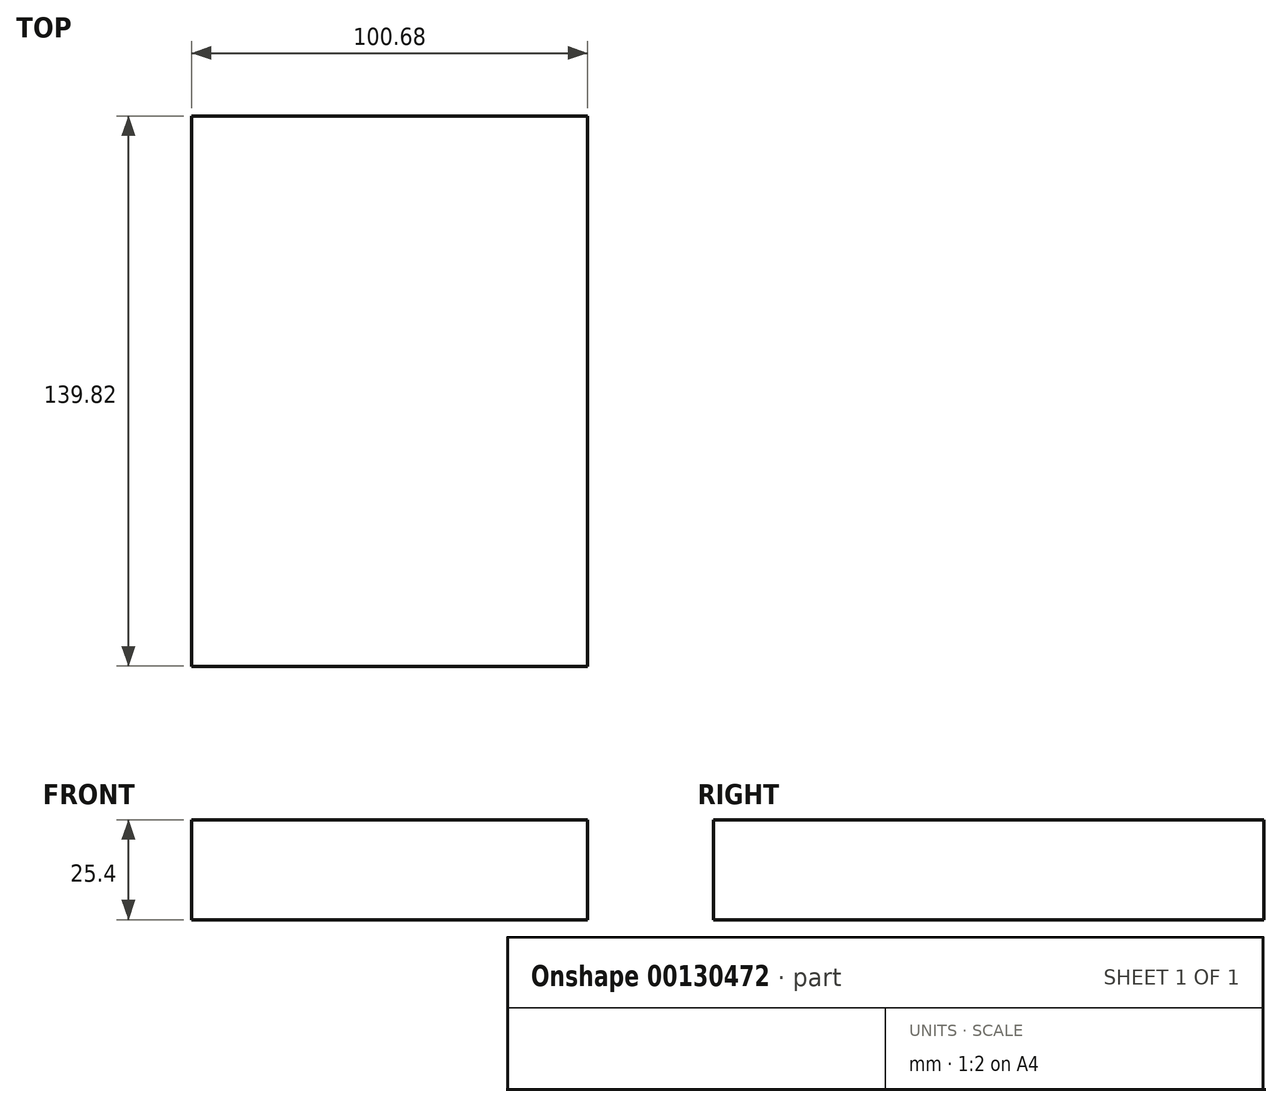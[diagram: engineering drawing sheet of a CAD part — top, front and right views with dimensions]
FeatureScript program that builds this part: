
annotation { "Feature Type Name" : "Feature", "Feature Type Description" : "" }
export const myFeature = defineFeature(function(context is Context, id is Id, definition is map)
    precondition{}
    {
        {
            var Q0;
            Q0=qCreatedBy(makeId("Top.planeOp"),FACE);
            var sketch = newSketch(context, id + "F0", { "sketchPlane" : qUnion([Q0])});
            skLineSegment(sketch, "E0.bottom", {"start": v(-54.6, -68.28) * mm, "end": v(46.08, -68.28) * mm});
            skLineSegment(sketch, "E0.top", {"start": v(-54.6, 71.54) * mm, "end": v(46.08, 71.54) * mm});
            skLineSegment(sketch, "E0.left", {"start": v(-54.6, -68.28) * mm, "end": v(-54.6, 71.54) * mm});
            skLineSegment(sketch, "E0.right", {"start": v(46.08, -68.28) * mm, "end": v(46.08, 71.54) * mm});
            skSolve(sketch);
        }
        {
            var Q0;
            Q0=makeQuery(id+"F0.imprint","IMPRINT",FACE,{"disambiguationData":[TD([[makeQuery(id+"F0.imprint","IMPRINT",EDGE,{"derivedFrom":sQuery(id+"F0.wireOp",EDGE,"E0.bottom")}),1.0]])]});
            extrude(context, id + "F1", {"entities" : qUnion([Q0]), "depth" : 25.4 * mm});
        }
    });
